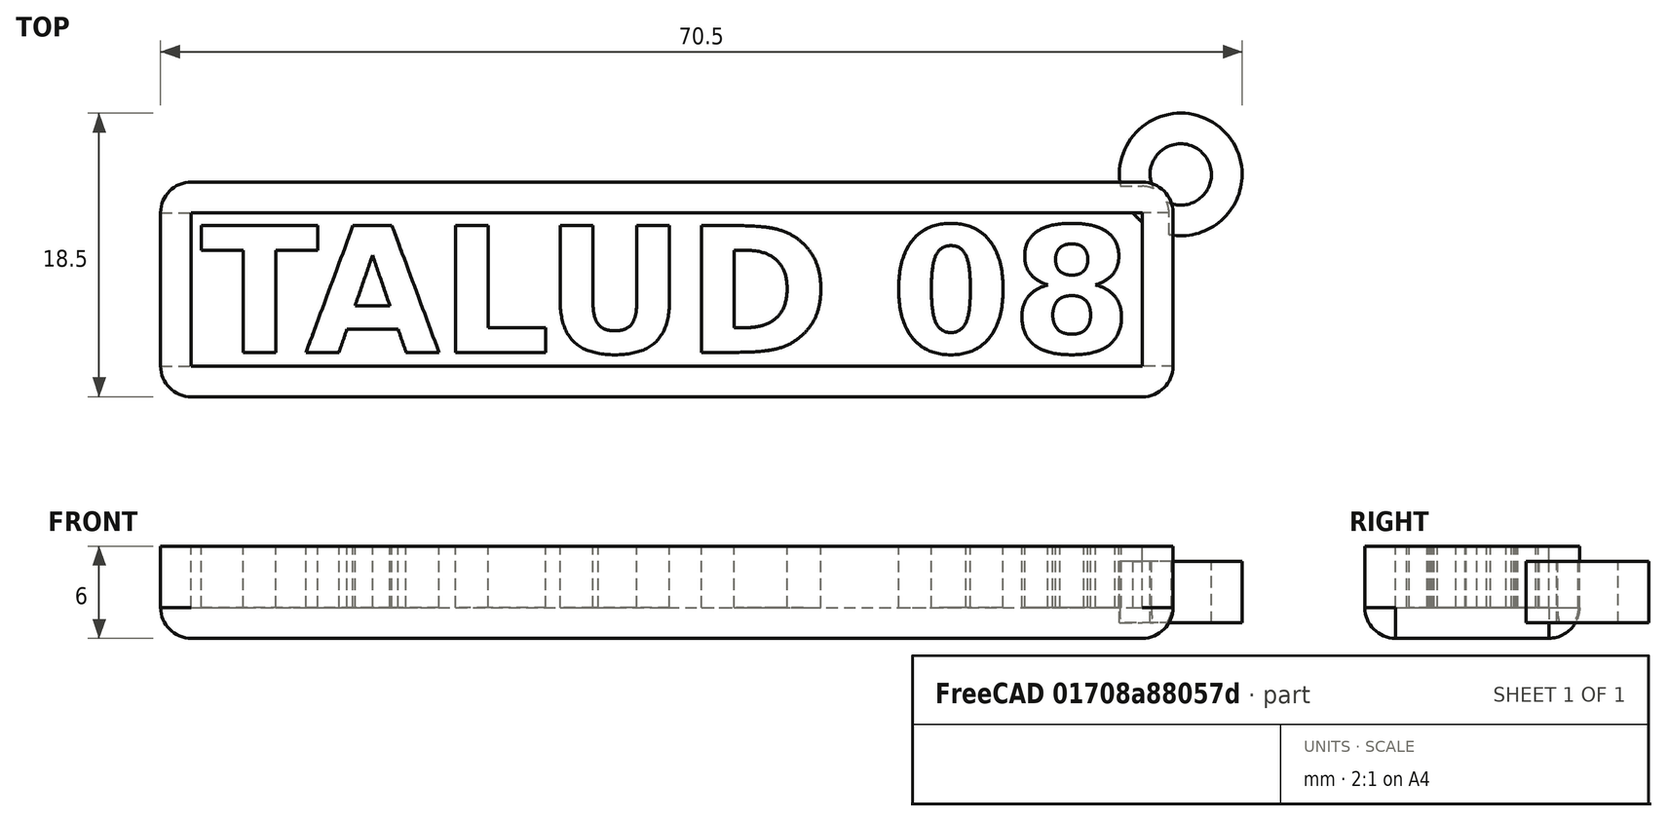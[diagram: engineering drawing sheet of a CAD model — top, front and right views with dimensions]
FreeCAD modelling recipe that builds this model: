
FCSTD DOCUMENT  (FreeCAD 0.16R6706 (Git))
Label: llavero
License: All rights reserved
LicenseURL: http://en.wikipedia.org/wiki/All_rights_reserved
objects: Part::Feature×12, Part::Extrusion×12, Part::Cut×6, Drawing::FeatureViewPart×3, Part::MultiFuse×2, Part::Cylinder×2, Part::Box×1, Part::Thickness×1, Drawing::FeaturePage×1
note: 36 computed .brp shape members not serialized (recipe doc carries the construction recipe); baked Part::Feature solids carry a one-line shape summary decoded from their .brp

FEATURE [Part::Feature] path3341
  shape: bbox 7.616 x 8.264 x 2e-07 mm, 0 faces, 0 solids (baked)
FEATURE [Part::Feature] path3343
  shape: bbox 8.662 x 8.264 x 2e-07 mm, 0 faces, 0 solids (baked)
FEATURE [Part::Feature] path3343001
  shape: bbox 2.264 x 3.288 x 2e-07 mm, 0 faces, 0 solids (baked)
FEATURE [Part::Feature] path3345
  shape: bbox 5.873 x 8.264 x 2e-07 mm, 0 faces, 0 solids (baked)
FEATURE [Part::Feature] path3347
  shape: bbox 7.124 x 8.424 x 2e-07 mm, 0 faces, 0 solids (baked)
FEATURE [Part::Feature] path3349
  shape: bbox 3.448 x 5.042 x 2e-07 mm, 0 faces, 0 solids (baked)
FEATURE [Part::Feature] path3349001
  shape: bbox 7.777 x 8.264 x 2e-07 mm, 0 faces, 0 solids (baked)
FEATURE [Part::Feature] path3351
  shape: bbox 2.541 x 5.668 x 2e-07 mm, 0 faces, 0 solids (baked)
FEATURE [Part::Feature] path3351001
  shape: bbox 6.803 x 8.574 x 2e-07 mm, 0 faces, 0 solids (baked)
FEATURE [Part::Feature] path3353
  shape: bbox 2.463 x 2.518 x 2e-07 mm, 0 faces, 0 solids (baked)
FEATURE [Part::Feature] path3353001
  shape: bbox 6.493 x 8.574 x 2e-07 mm, 0 faces, 0 solids (baked)
FEATURE [Part::Feature] path3353002
  shape: bbox 2.098 x 2.042 x 2e-07 mm, 0 faces, 0 solids (baked)
FEATURE [Part::Extrusion] Extrude
  Base = -> path3341
  Dir = (0,0,5)
  Solid = true
FEATURE [Part::Extrusion] Extrude001
  Base = -> path3343
  Dir = (0,0,5)
  Solid = true
FEATURE [Part::Extrusion] Extrude002
  Base = -> path3343001
  Dir = (0,0,5)
  Solid = true
FEATURE [Part::Extrusion] Extrude003
  Base = -> path3345
  Dir = (0,0,5)
  Solid = true
FEATURE [Part::Extrusion] Extrude004
  Base = -> path3347
  Dir = (0,0,5)
  Solid = true
FEATURE [Part::Extrusion] Extrude005
  Base = -> path3349
  Dir = (0,0,5)
  Solid = true
FEATURE [Part::Extrusion] Extrude006
  Base = -> path3349001
  Dir = (0,0,5)
  Solid = true
FEATURE [Part::Extrusion] Extrude007
  Base = -> path3351
  Dir = (0,0,5)
  Solid = true
FEATURE [Part::Extrusion] Extrude008
  Base = -> path3351001
  Dir = (0,0,5)
  Solid = true
FEATURE [Part::Extrusion] Extrude009
  Base = -> path3353
  Dir = (0,0,5)
  Solid = true
FEATURE [Part::Extrusion] Extrude010
  Base = -> path3353001
  Dir = (0,0,5)
  Solid = true
FEATURE [Part::Extrusion] Extrude011
  Base = -> path3353002
  Dir = (0,0,5)
  Solid = true
FEATURE [Part::Cut] Cut
  Base = -> Extrude006
  Tool = -> Extrude005
FEATURE [Part::Cut] Cut001
  Base = -> Extrude008
  Tool = -> Extrude007
FEATURE [Part::Cut] Cut002
  Base = -> Extrude010
  Tool = -> Extrude011
FEATURE [Part::Cut] Cut003
  Base = -> Cut002
  Tool = -> Extrude009
FEATURE [Part::Cut] Cut004
  Base = -> Extrude001
  Tool = -> Extrude002
FEATURE [Part::MultiFuse] Fusion  label="letras"
  Shapes = -> [Extrude,Cut001,Cut,Extrude003,Extrude004,Cut004,Cut003]
FEATURE [Part::Box] Box  label="Cubo"
  Height = 4
  Length = 62
  Placement = pos=(-28,-6,1) rot=(0,0,1;0rad)
  Width = 10
FEATURE [Part::Thickness] Thickness  label="marco"
  Faces = -> Box [Face6]
  Intersection = false
  Join = 0
  Mode = 0
  SelfIntersection = false
  Value = 2
FEATURE [Part::Cylinder] Cylinder  label="Cilindro"
  Angle = 360
  Height = 4
  Radius = 4
FEATURE [Part::Cylinder] Cylinder001  label="Cilindro001"
  Angle = 360
  Height = 10
  Placement = pos=(0,0,-3) rot=(0,0,1;0rad)
  Radius = 2
FEATURE [Part::Cut] Cut005  label="aro"
  Base = -> Cylinder
  Placement = pos=(36.5,6.5,0) rot=(0,0,1;0rad)
  Tool = -> Cylinder001
FEATURE [Part::MultiFuse] Fusion001
  Shapes = -> [Cut005,Thickness,Fusion]
FEATURE [Drawing::FeatureViewPart] Ortho  label="Ortho_0_0"
  Direction = (1,0,0)
  HiddenWidth = 0.15
  LineWidth = 0.35
  Rotation = -90
  ShowHiddenLines = false
  ShowSmoothLines = false
  Source = -> Fusion001
  Tolerance = 0.05
  ViewResult = <blob: 2300 chars omitted>
  Visible = true
  X = 100
  Y = 170
FEATURE [Drawing::FeatureViewPart] Ortho001  label="Ortho_0_1"
  Direction = (0,0,1)
  HiddenWidth = 0.15
  LineWidth = 0.35
  Rotation = 90
  ShowHiddenLines = false
  ShowSmoothLines = false
  Source = -> Fusion001
  Tolerance = 0.05
  ViewResult = <blob: 15318 chars omitted>
  Visible = true
  X = 100
  Y = 90
FEATURE [Drawing::FeatureViewPart] Ortho002  label="Ortho_0_-1"
  Direction = (0,0,-1)
  HiddenWidth = 0.15
  LineWidth = 0.35
  Rotation = 90
  ShowHiddenLines = false
  ShowSmoothLines = false
  Source = -> Fusion001
  Tolerance = 0.05
  ViewResult = <g id="Ortho_0_-1"\n   transform="rotate(90,200,100) translate(200,100) scale(1,1)"\n  >\n<g   stroke="rgb(0, 0, 0)"\n   stroke-width="0.35"\n   stroke-linecap="butt"\n   stroke-linejoin="miter"\n   fill="none"\n   transform="scale(1,-1)"\n  >\n<path id= "1" d=" M 30 -6 L 30 4 " />\n<path id= "2" d=" M 28 -8 L -34 -8 " />\n<path id= "3" d=" M -36 -6 L -36 2.53137 " />\n<path id= "4" d=" M 28 6 L -32.5314 6 " />\n<path d="M30 -6 A2 2 0 0 0 28 -8" /><path d="M-36 -6 A2 2 0 0 1 -34 -8" /><path d="M-35.8934,2.54626 Q-35.8151,2.55823 -35.7321,2.57441 " /><path id= "8" d=" M -35.7321 2.57441 L -35.7321 4 " />\n<path d="M-35.9114 4.58856 A2 2 0 0 0 -34.5886 5.91144" /><path d="M-34.711,5.60586 L-34.7287,5.57131 " /><path d="M-34.7287 5.57131 A1.73205 1.73205 0 0 0 -34 5.73205" /><path d="M-35.7321 4 A1.73205 1.73205 0 0 0 -35.5713 4.72869" /><path d="M-35.8213,4.61868 Q-35.9087,4.58853 -35.9114,4.58856 " /><path d="M-32.5463,5.89344 Q-32.5582,5.81508 -32.5744,5.73205 " /><path id= "15" d=" M -32.5744 5.73205 L -34 5.73205 " />\n<path d="M30 4 A2 2 0 0 1 28 6" /><path d="M-35.7321 2.57441 A4 4 0 0 0 -40.5 6.5" /><path d="M-35.5713 4.72869 A2 2 0 0 0 -38.5 6.5" /><path d="M-38.5 6.5 A2 2 0 1 0 -34.7287 5.57131" /><path d="M-40.5 6.5 A4 4 0 1 0 -32.5744 5.73205" /></g>\n</g>
  Visible = true
  X = 200
  Y = 100
FEATURE [Drawing::FeaturePage] Page
  EditableTexts = Designed by Name | Date | Scale | Weight | Title | Subtitle | Drawing number | Sheet
  Group = -> [Ortho,Ortho001,Ortho002]
